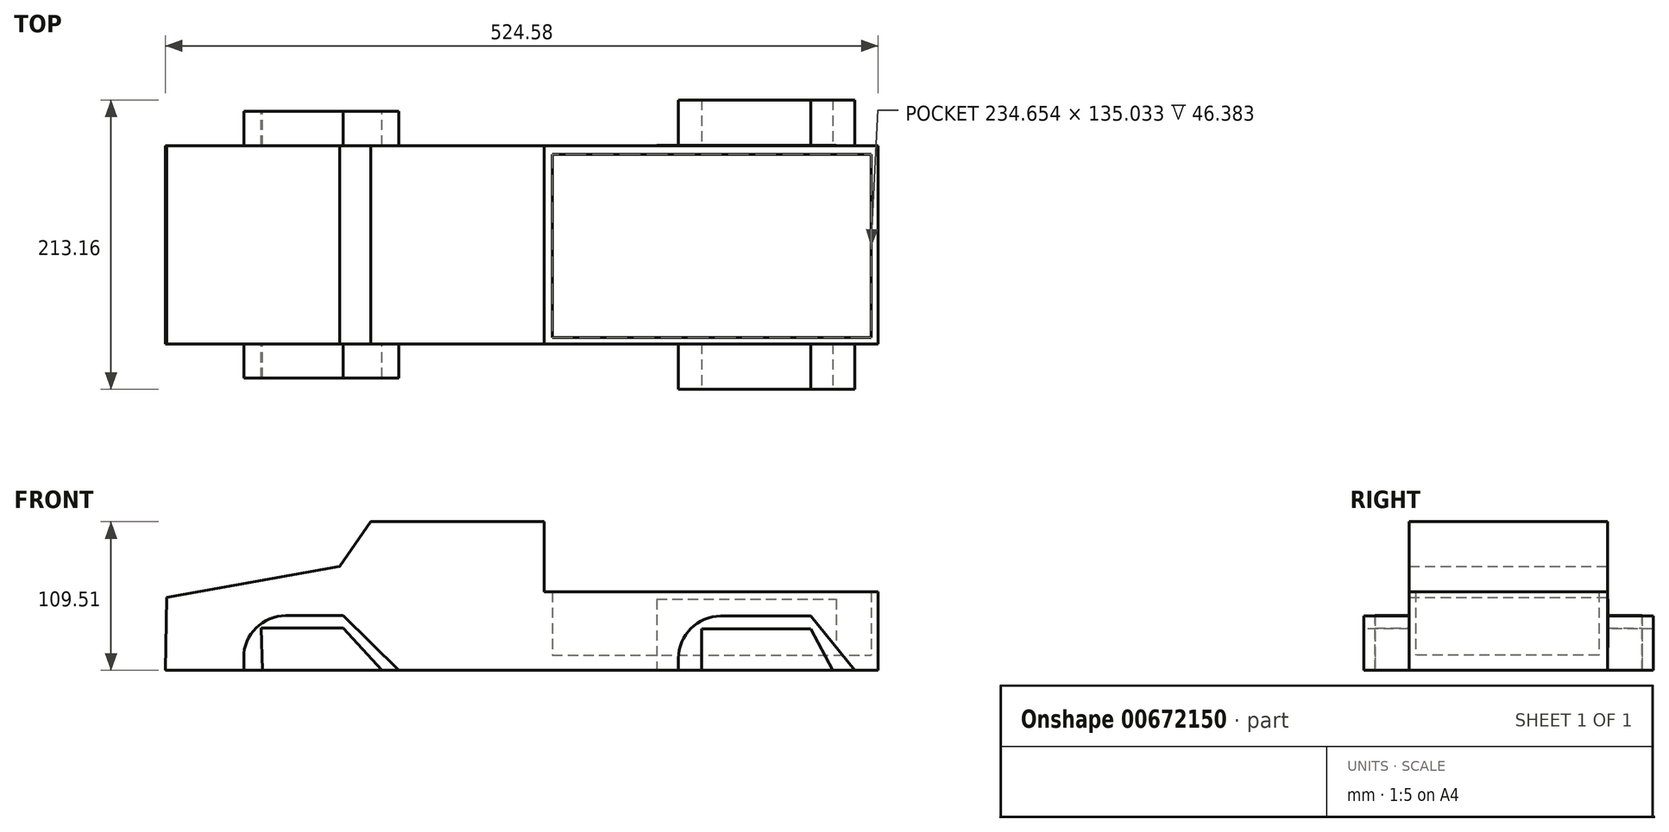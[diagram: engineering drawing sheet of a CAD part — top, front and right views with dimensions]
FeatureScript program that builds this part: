
annotation { "Feature Type Name" : "Feature", "Feature Type Description" : "" }
export const myFeature = defineFeature(function(context is Context, id is Id, definition is map)
    precondition{}
    {
        {
            var Q0;
            Q0=qCreatedBy(makeId("Front.planeOp"),FACE);
            var sketch = newSketch(context, id + "F0", { "sketchPlane" : qUnion([Q0])});
            skLineSegment(sketch, "E0", {"start": v(-324.18, 53.86) * mm, "end": v(-196.87, 76.73) * mm});
            skLineSegment(sketch, "E1", {"start": v(-196.87, 76.73) * mm, "end": v(-173.96, 109.5) * mm});
            skLineSegment(sketch, "E2", {"start": v(-173.96, 109.5) * mm, "end": v(-46.36, 109.5) * mm});
            skLineSegment(sketch, "E3", {"start": v(-46.36, 109.5) * mm, "end": v(-46.36, 57.7) * mm});
            skLineSegment(sketch, "E4", {"start": v(-46.36, 57.7) * mm, "end": v(199.4, 57.7) * mm});
            skLineSegment(sketch, "E5", {"start": v(199.4, 57.7) * mm, "end": v(199.4, 0) * mm});
            skLineSegment(sketch, "E6", {"start": v(199.4, 0) * mm, "end": v(140.16, 0) * mm});
            skLineSegment(sketch, "E7", {"start": v(140.16, 0) * mm, "end": v(141.22, 33.56) * mm});
            skLineSegment(sketch, "E8", {"start": v(141.22, 33.56) * mm, "end": v(76.52, 33.56) * mm});
            skPoint(sketch, "E8.endSnap0", {"position": v(76.52, 57.7) * mm});
            skLineSegment(sketch, "E9", {"start": v(76.52, 33.56) * mm, "end": v(76.52, 0) * mm});
            skLineSegment(sketch, "E10", {"start": v(76.52, 0) * mm, "end": v(-232.16, 0) * mm});
            skLineSegment(sketch, "E11", {"start": v(-232.16, 0) * mm, "end": v(-233.21, 34.44) * mm});
            skLineSegment(sketch, "E12", {"start": v(-233.21, 34.44) * mm, "end": v(-285.04, 34.44) * mm});
            skLineSegment(sketch, "E13", {"start": v(-285.04, 34.44) * mm, "end": v(-285.04, 0) * mm});
            skLineSegment(sketch, "E14", {"start": v(-285.04, 0) * mm, "end": v(-325.18, 0) * mm});
            skLineSegment(sketch, "E15", {"start": v(-325.18, 0) * mm, "end": v(-324.18, 53.86) * mm});
            skSolve(sketch);
        }
        {
            var Q0;
            Q0=makeQuery(id+"F0.imprint","IMPRINT",FACE,{"disambiguationData":[TD([[makeQuery(id+"F0.imprint","IMPRINT",EDGE,{"derivedFrom":sQuery(id+"F0.wireOp",EDGE,"E0")}),-1.0]])]});
            extrude(context, id + "F1", {"entities" : qUnion([Q0]), "endBound" : BoundingType.SYMMETRIC, "depth" : 146.03 * mm, "offsetDistance" : 25.4 * mm});
        }
        {
            var Q0;
            Q0=makeQuery(id+"F1.opExtrude","SWEPT_FACE",FACE,{"disambiguationData":[OSD([sQuery(id+"F0.wireOp",EDGE,"E10")])]});
            var sketch = newSketch(context, id + "F2", { "sketchPlane" : qUnion([Q0])});
            skLineSegment(sketch, "E16.bottom", {"start": v(-298.68, 73.01) * mm, "end": v(-193.91, 73.01) * mm});
            skLineSegment(sketch, "E16.top", {"start": v(-298.68, -73.01) * mm, "end": v(-193.91, -73.01) * mm});
            skLineSegment(sketch, "E16.left", {"start": v(-298.68, 73.01) * mm, "end": v(-298.68, -73.01) * mm});
            skLineSegment(sketch, "E16.right", {"start": v(-193.91, 73.01) * mm, "end": v(-193.91, -73.01) * mm});
            skLineSegment(sketch, "E17.bottom", {"start": v(36.48, 73.01) * mm, "end": v(168.7, 73.01) * mm});
            skLineSegment(sketch, "E17.top", {"start": v(36.48, -73.05) * mm, "end": v(168.7, -73.05) * mm});
            skLineSegment(sketch, "E17.left", {"start": v(36.48, 73.01) * mm, "end": v(36.48, -73.05) * mm});
            skLineSegment(sketch, "E17.right", {"start": v(168.7, 73.01) * mm, "end": v(168.7, -73.05) * mm});
            skSolve(sketch);
        }
        {
            var Q0;
            Q0 = qSketchRegion(id + "F2", true);
            extrude(context, id + "F3", {"entities" : qUnion([Q0]), "operationType" : NewBodyOperationType.ADD, "oppositeDirection" : true, "depth" : 52.42 * mm, "offsetDistance" : 25.4 * mm});
        }
        {
            var Q0;
            Q0=qCreatedBy(makeId("Front.planeOp"),FACE);
            var sketch = newSketch(context, id + "F4", { "sketchPlane" : qUnion([Q0])});
            skLineSegment(sketch, "E18.bottom", {"start": v(-267.5, 40.32) * mm, "end": v(-194.18, 40.32) * mm});
            skLineSegment(sketch, "E18.top", {"start": v(-267.5, 31.22) * mm, "end": v(-194.18, 31.22) * mm});
            skLineSegment(sketch, "E18.left", {"start": v(-267.5, 40.32) * mm, "end": v(-267.5, 31.22) * mm});
            skLineSegment(sketch, "E18.right", {"start": v(-194.18, 40.32) * mm, "end": v(-194.18, 31.22) * mm});
            skLineSegment(sketch, "E19", {"start": v(-194.18, 31.22) * mm, "end": v(-165.9, 0) * mm});
            skLineSegment(sketch, "E20", {"start": v(-165.9, 0) * mm, "end": v(-153.45, 0) * mm});
            skLineSegment(sketch, "E21", {"start": v(-153.45, 0) * mm, "end": v(-194.18, 40.32) * mm});
            skLineSegment(sketch, "E22", {"start": v(-267.5, 31.22) * mm, "end": v(-267.5, 0) * mm});
            skLineSegment(sketch, "E23", {"start": v(-267.5, 0) * mm, "end": v(-253.6, 0) * mm});
            skLineSegment(sketch, "E24", {"start": v(-253.6, 0) * mm, "end": v(-254.55, 31.22) * mm});
            skLineSegment(sketch, "E25", {"start": v(-254.55, 31.22) * mm, "end": v(-267.5, 31.22) * mm});
            skSolve(sketch);
        }
        {
            var Q0;
            Q0 = qSketchRegion(id + "F4", true);
            extrude(context, id + "F5", {"entities" : qUnion([Q0]), "operationType" : NewBodyOperationType.ADD, "endBound" : BoundingType.SYMMETRIC, "depth" : 196.43 * mm, "offsetDistance" : 25.4 * mm});
        }
        {
            var Q0;
            Q0=qCreatedBy(makeId("Front.planeOp"),FACE);
            var sketch = newSketch(context, id + "F6", { "sketchPlane" : qUnion([Q0])});
            skLineSegment(sketch, "E26.bottom", {"start": v(52.55, 30.6) * mm, "end": v(149.91, 30.6) * mm});
            skLineSegment(sketch, "E26.top", {"start": v(52.55, 39.95) * mm, "end": v(149.91, 39.95) * mm});
            skLineSegment(sketch, "E26.left", {"start": v(52.55, 30.6) * mm, "end": v(52.55, 39.95) * mm});
            skLineSegment(sketch, "E26.right", {"start": v(149.91, 30.6) * mm, "end": v(149.91, 39.95) * mm});
            skLineSegment(sketch, "E27", {"start": v(149.91, 39.95) * mm, "end": v(182.35, 0) * mm});
            skLineSegment(sketch, "E28", {"start": v(182.35, 0) * mm, "end": v(166.13, 0) * mm});
            skPoint(sketch, "E28.endSnap0", {"position": v(166.13, 19.98) * mm});
            skLineSegment(sketch, "E29", {"start": v(166.13, 0) * mm, "end": v(149.91, 30.6) * mm});
            skLineSegment(sketch, "E30", {"start": v(52.55, 30.6) * mm, "end": v(52.55, 0) * mm});
            skLineSegment(sketch, "E31", {"start": v(52.55, 0) * mm, "end": v(69.5, 0) * mm});
            skLineSegment(sketch, "E32", {"start": v(69.5, 0) * mm, "end": v(69.5, 30.6) * mm});
            skLineSegment(sketch, "E33", {"start": v(69.5, 30.6) * mm, "end": v(52.55, 30.6) * mm});
            skSolve(sketch);
        }
        {
            var Q0;
            Q0 = qSketchRegion(id + "F6", true);
            extrude(context, id + "F7", {"entities" : qUnion([Q0]), "operationType" : NewBodyOperationType.ADD, "endBound" : BoundingType.SYMMETRIC, "oppositeDirection" : true, "depth" : 213.17 * mm, "offsetDistance" : 25.4 * mm});
        }
        {
            var Q0;
            Q0=qCreatedBy(makeId("Top.planeOp"),FACE);
            var sketch = newSketch(context, id + "F8", { "sketchPlane" : qUnion([Q0])});
            skLineSegment(sketch, "E34.bottom", {"start": v(-40.4, 66.51) * mm, "end": v(194.26, 66.51) * mm});
            skLineSegment(sketch, "E34.top", {"start": v(-40.4, -68.52) * mm, "end": v(194.26, -68.52) * mm});
            skLineSegment(sketch, "E34.left", {"start": v(-40.4, 66.51) * mm, "end": v(-40.4, -68.52) * mm});
            skLineSegment(sketch, "E34.right", {"start": v(194.26, 66.51) * mm, "end": v(194.26, -68.52) * mm});
            skSolve(sketch);
        }
        {
            var Q0;
            Q0 = qSketchRegion(id + "F8", true);
            extrude(context, id + "F9", {"entities" : qUnion([Q0]), "operationType" : NewBodyOperationType.REMOVE, "depth" : 105.92 * mm, "offsetDistance" : 25.4 * mm});
        }
        {
            var Q0;
            Q0=qCreatedBy(makeId("Top.planeOp"),FACE);
            var sketch = newSketch(context, id + "F10", { "sketchPlane" : qUnion([Q0])});
            skLineSegment(sketch, "E35.bottom", {"start": v(-42.98, 69.71) * mm, "end": v(196.17, 69.71) * mm});
            skLineSegment(sketch, "E35.top", {"start": v(-42.98, -70.4) * mm, "end": v(196.17, -70.4) * mm});
            skLineSegment(sketch, "E35.left", {"start": v(-42.98, 69.71) * mm, "end": v(-42.98, -70.4) * mm});
            skLineSegment(sketch, "E35.right", {"start": v(196.17, 69.71) * mm, "end": v(196.17, -70.4) * mm});
            skSolve(sketch);
        }
        {
            var Q0;
            Q0 = qSketchRegion(id + "F10", true);
            extrude(context, id + "F11", {"entities" : qUnion([Q0]), "operationType" : NewBodyOperationType.ADD, "depth" : 11.32 * mm, "offsetDistance" : 25.4 * mm});
        }
        {
            var Q0;
            {var subQ1=sQuery(id+"F6.wireOp",EDGE,"E26.left");var subQ2=sQuery(id+"F6.wireOp",EDGE,"E26.top");Q0=makeQuery(id+"F7.boolean.opBoolean","SPLIT",EDGE,{"disambiguationData":[TD([makeQuery(id+"F3.opExtrude","SWEPT_FACE",FACE,{"disambiguationData":[OSD([sQuery(id+"F2.wireOp",EDGE,"E17.top")])]})])],"derivedFrom":makeQuery(id+"F7.opExtrude","SWEPT_EDGE",EDGE,{"disambiguationData":[OSD([subQ2,subQ1])]})});}
            var Q1;
            {var subQ1=sQuery(id+"F4.wireOp",EDGE,"E18.left");var subQ2=sQuery(id+"F4.wireOp",EDGE,"E18.bottom");Q1=makeQuery(id+"F5.boolean.opBoolean","SPLIT",EDGE,{"disambiguationData":[TD([makeQuery(id+"F3.opExtrude","SWEPT_FACE",FACE,{"disambiguationData":[OSD([sQuery(id+"F2.wireOp",EDGE,"E16.top")])]})])],"derivedFrom":makeQuery(id+"F5.opExtrude","SWEPT_EDGE",EDGE,{"disambiguationData":[OSD([subQ2,subQ1])]})});}
            var Q2;
            {var subQ0=sQuery(id+"F4.wireOp",EDGE,"E18.bottom");var subQ2=sQuery(id+"F4.wireOp",EDGE,"E18.left");Q2=makeQuery(id+"F5.boolean.opBoolean","SPLIT",EDGE,{"disambiguationData":[TD([makeQuery(id+"F3.opExtrude","SWEPT_FACE",FACE,{"disambiguationData":[OSD([sQuery(id+"F2.wireOp",EDGE,"E16.bottom")])]})])],"derivedFrom":makeQuery(id+"F5.opExtrude","SWEPT_EDGE",EDGE,{"disambiguationData":[OSD([subQ0,subQ2])]})});}
            var Q3;
            {var subQ1=sQuery(id+"F6.wireOp",EDGE,"E26.left");var subQ2=sQuery(id+"F6.wireOp",EDGE,"E26.top");Q3=makeQuery(id+"F7.boolean.opBoolean","SPLIT",EDGE,{"disambiguationData":[TD([makeQuery(id+"F3.opExtrude","SWEPT_FACE",FACE,{"disambiguationData":[OSD([sQuery(id+"F2.wireOp",EDGE,"E16.bottom")])]})])],"derivedFrom":makeQuery(id+"F7.opExtrude","SWEPT_EDGE",EDGE,{"disambiguationData":[OSD([subQ2,subQ1])]})});}
            fillet(context, id + "F12", {"entities" : qUnion([Q0, Q1, Q2, Q3]), "radius" : 31.09 * mm, "tangentPropagation" : true, "allowEdgeOverflow" : false});
        }
    });
